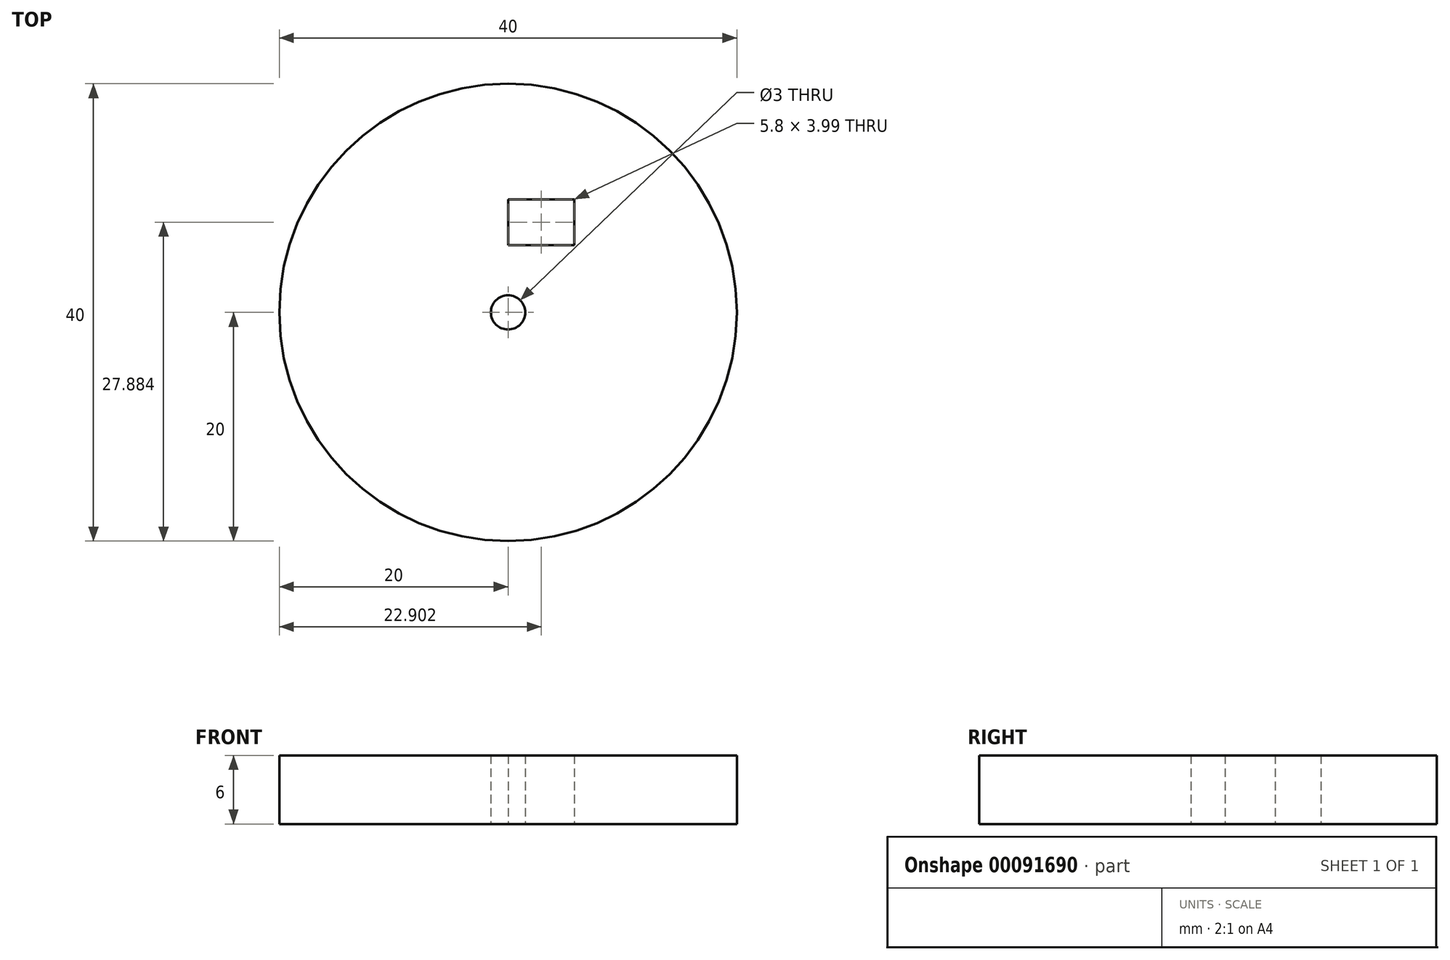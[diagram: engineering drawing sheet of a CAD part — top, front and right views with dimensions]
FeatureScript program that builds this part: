
annotation { "Feature Type Name" : "Feature", "Feature Type Description" : "" }
export const myFeature = defineFeature(function(context is Context, id is Id, definition is map)
    precondition{}
    {
        {
            var Q0;
            Q0=qCreatedBy(makeId("Top.planeOp"),FACE);
            var sketch = newSketch(context, id + "F0", { "sketchPlane" : qUnion([Q0])});
            skCircle(sketch, "E0", {"center": v(0, 0) * mm, "radius": 20 * mm});
            skCircle(sketch, "E1", {"center": v(0, 0) * mm, "radius": 1.5 * mm});
            skLineSegment(sketch, "E2.bottom", {"start": v(0, 9.88) * mm, "end": v(5.8, 9.88) * mm});
            skLineSegment(sketch, "E2.top", {"start": v(0, 5.89) * mm, "end": v(5.8, 5.89) * mm});
            skLineSegment(sketch, "E2.left", {"start": v(0, 9.88) * mm, "end": v(0, 5.89) * mm});
            skLineSegment(sketch, "E2.right", {"start": v(5.8, 9.88) * mm, "end": v(5.8, 5.89) * mm});
            skSolve(sketch);
        }
        {
            var Q0;
            Q0 = qSketchRegion(id + "F0", true);
            extrude(context, id + "F1", {"entities" : qUnion([Q0]), "depth" : 6 * mm});
        }
    });
